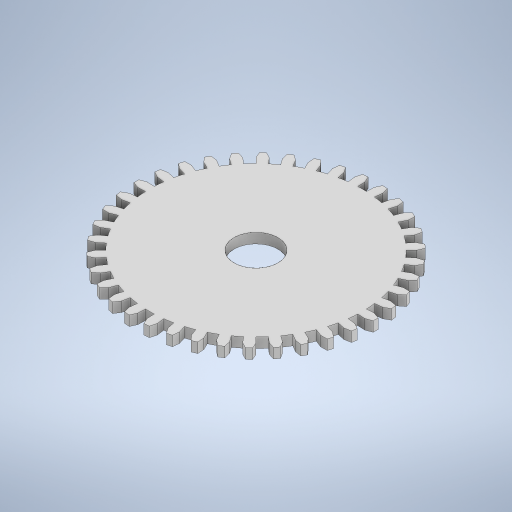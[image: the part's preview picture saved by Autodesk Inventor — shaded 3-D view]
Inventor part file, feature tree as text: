
AUTODESK INVENTOR PART (.ipt)
format: ipt  version: 2024.1 (Build 281209000, 209)  size: 585,728 bytes
history: native  units: mm
features: other x1, extrude x1, sketch x1
ambient origin geometry x8: Origin, YZ Plane, XZ Plane, XY Plane, X Axis, Y Axis, Z Axis, Center Point
bodies: Body1 (feature_tree)
feature tree (3):
  other  "ソリッド1"
  extrude  "押し出し1"  Depth=114.0mm
  sketch  "スケッチ1"
